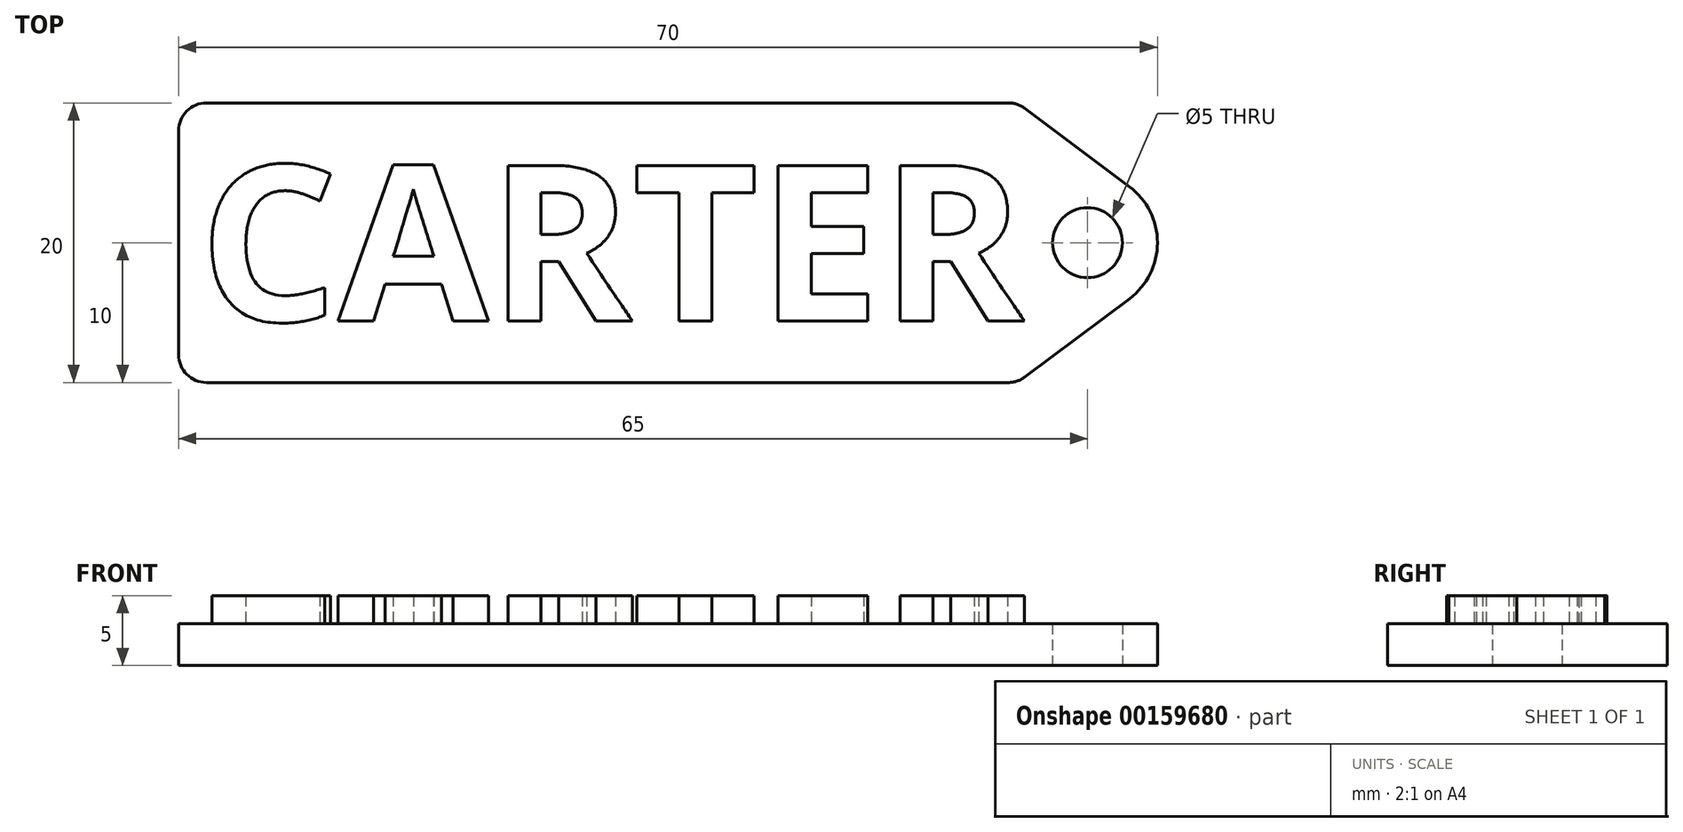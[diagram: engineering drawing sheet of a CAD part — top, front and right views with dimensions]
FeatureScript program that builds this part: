
annotation { "Feature Type Name" : "Feature", "Feature Type Description" : "" }
export const myFeature = defineFeature(function(context is Context, id is Id, definition is map)
    precondition{}
    {
        {
            var Q0;
            Q0=qCreatedBy(makeId("Top.planeOp"),FACE);
            var sketch = newSketch(context, id + "F0", { "sketchPlane" : qUnion([Q0])});
            skLineSegment(sketch, "E0.bottom", {"start": v(29.33, -10) * mm, "end": v(-28, -10) * mm});
            skLineSegment(sketch, "E0.top", {"start": v(29.33, 10) * mm, "end": v(-28, 10) * mm});
            skLineSegment(sketch, "E0.left", {"start": v(30, -10) * mm, "end": v(30, 10) * mm, "construction": true});
            skLineSegment(sketch, "E0.right", {"start": v(-30, -8) * mm, "end": v(-30, 8) * mm});
            skPoint(sketch, "E0.middle", {"position": v(0, 0) * mm});
            skCircle(sketch, "E1", {"center": v(35, 0) * mm, "radius": 2.5 * mm});
            skLineSegment(sketch, "E2", {"start": v(30.53, 9.6) * mm, "end": v(38, 4) * mm});
            skArc(sketch, "E3", {"start": v(40, 0) * mm, "mid": v(39.47, 2.24) * mm, "end": v(38, 4) * mm});
            skLineSegment(sketch, "E4.MirrorCS", {"start": v(30.53, -9.6) * mm, "end": v(38, -4) * mm});
            skArc(sketch, "E5.MirrorCS", {"start": v(40, 0) * mm, "mid": v(39.47, -2.24) * mm, "end": v(38, -4) * mm});
            skPoint(sketch, "E6.visualSharp", {"position": v(-30, 10) * mm});
            skArc(sketch, "E6.filletArc", {"start": v(-28, 10) * mm, "mid": v(-29.41, 9.41) * mm, "end": v(-30, 8) * mm});
            skPoint(sketch, "E7.visualSharp", {"position": v(-30, -10) * mm});
            skArc(sketch, "E7.filletArc", {"start": v(-30, -8) * mm, "mid": v(-29.41, -9.41) * mm, "end": v(-28, -10) * mm});
            skPoint(sketch, "E8.visualSharp", {"position": v(30, 10) * mm});
            skArc(sketch, "E8.filletArc", {"start": v(30.53, 9.6) * mm, "mid": v(29.97, 9.9) * mm, "end": v(29.33, 10) * mm});
            skPoint(sketch, "E9.visualSharp", {"position": v(30, -10) * mm});
            skArc(sketch, "E9.filletArc", {"start": v(29.33, -10) * mm, "mid": v(29.97, -9.9) * mm, "end": v(30.53, -9.6) * mm});
            skSolve(sketch);
        }
        {
            var Q0;
            Q0=makeQuery(id+"F0.imprint","IMPRINT",FACE,{"disambiguationData":[TD([[makeQuery(id+"F0.imprint","IMPRINT",EDGE,{"derivedFrom":sQuery(id+"F0.wireOp",EDGE,"E0.bottom")}),-1.0]])]});
            extrude(context, id + "F1", {"entities" : qUnion([Q0]), "depth" : 3 * mm});
        }
        {
            var Q0;
            Q0=makeQuery(id+"F1.opExtrude","CAP_FACE",FACE,{"disambiguationData":[OSD([sQuery(id+"F0.wireOp",EDGE,"E0.bottom"),sQuery(id+"F0.wireOp",EDGE,"E0.top"),sQuery(id+"F0.wireOp",EDGE,"E0.right"),sQuery(id+"F0.wireOp",EDGE,"E1"),sQuery(id+"F0.wireOp",EDGE,"E2"),sQuery(id+"F0.wireOp",EDGE,"E3"),sQuery(id+"F0.wireOp",EDGE,"E4.MirrorCS"),sQuery(id+"F0.wireOp",EDGE,"E5.MirrorCS"),sQuery(id+"F0.wireOp",EDGE,"E6.filletArc"),sQuery(id+"F0.wireOp",EDGE,"E7.filletArc"),sQuery(id+"F0.wireOp",EDGE,"E8.filletArc"),sQuery(id+"F0.wireOp",EDGE,"E9.filletArc")])],"isStart":false});
            var sketch = newSketch(context, id + "F2", { "sketchPlane" : qUnion([Q0])});
            skText(sketch, "E10", { "text": "CARTER", "fontName": "OpenSans-Bold.ttf"});
            skPoint(sketch, "E11", {"position": v(-28.52, 0) * mm});
            const initialGuessF2  = {"E10": [-0.02852, -0.0056, 1, 0, 0.01122]};
            skSetInitialGuess(sketch, initialGuessF2);
            skSolve(sketch);
        }
        {
            var Q0;
            Q0=qSketchRegion(id+"F2",true);
            extrude(context, id + "F3", {"entities" : qUnion([Q0]), "operationType" : NewBodyOperationType.ADD, "depth" : 2 * mm});
        }
    });
